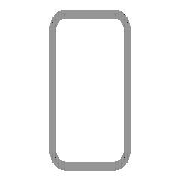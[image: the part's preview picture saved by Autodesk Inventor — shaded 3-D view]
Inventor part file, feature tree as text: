
AUTODESK INVENTOR PART (.ipt)
format: ipt  version: 2025 (Build 290162010, 162A)  size: 144,384 bytes
history: native  units: mm (DEFAULTED — no unit token found)
features: other x4, sketch x1, plane x1
ambient origin geometry x8: Origin, YZ Plane, XZ Plane, XY Plane, X Axis, Y Axis, Z Axis, Center Point
bodies: Solid1 (feature_tree), Body (feature_tree)
feature tree (6):
  parser-record x1  (decoder bookkeeping rows leaked as tree rows — omitted from the tree; the rows remain in map.json)
  other  "Driven Length"
  other  "Start Plane"
  other  "End Plane"
  sketch  "Sketch3"  dims[d3=3000.0mm d4=0.0mm d7=4.5mm d10=60.0mm d11=40.0mm d12=3.0mm d13=-0.0mm d14=3000.0mm d15=30.0mm d16=20.0mm d17=90.0deg d18=3000.0mm]
  plane  "Work Plane3"
